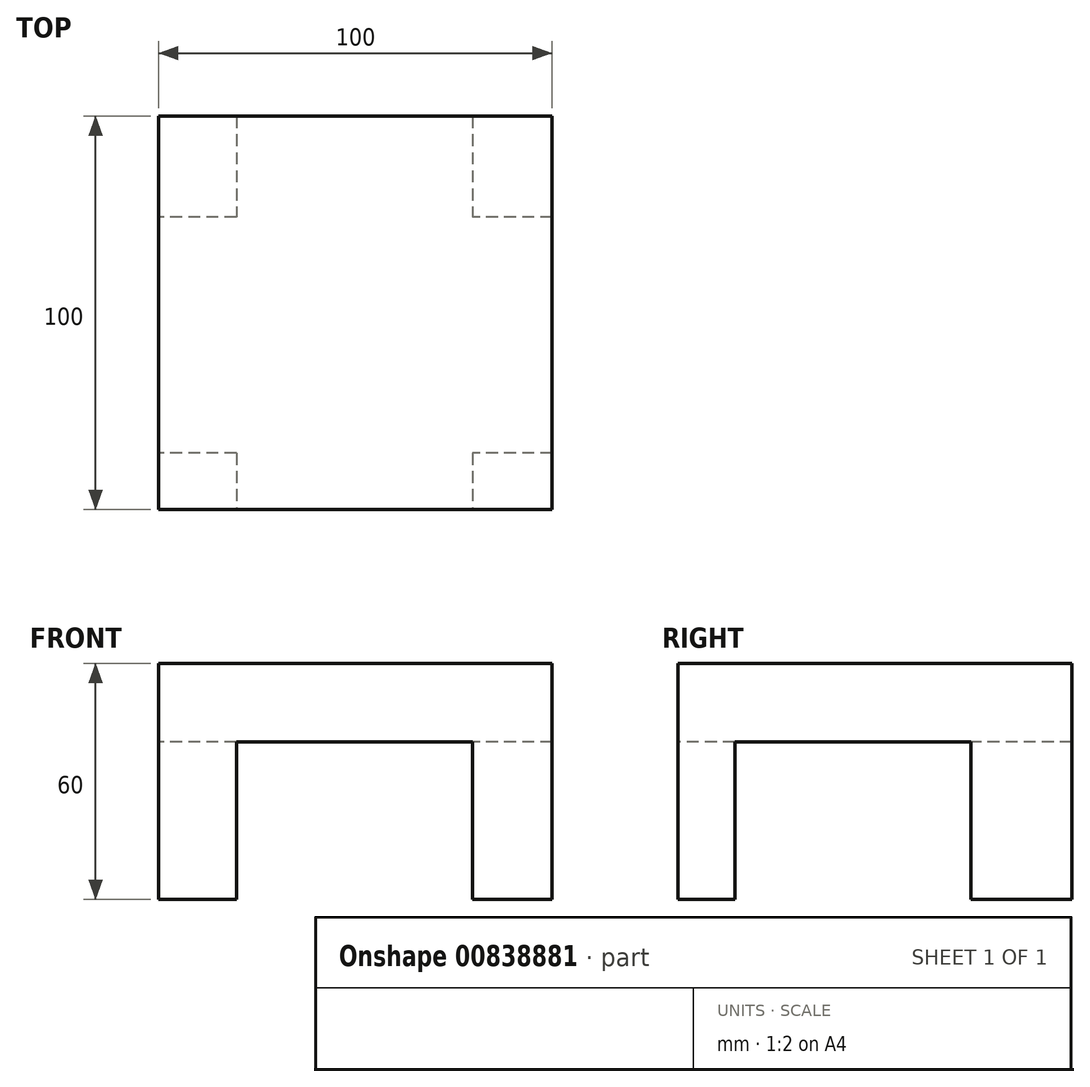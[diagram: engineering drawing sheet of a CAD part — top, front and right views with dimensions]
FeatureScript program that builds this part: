
annotation { "Feature Type Name" : "Feature", "Feature Type Description" : "" }
export const myFeature = defineFeature(function(context is Context, id is Id, definition is map)
    precondition{}
    {
        {
            var Q0;
            Q0=qCreatedBy(makeId("Top.planeOp"),FACE);
            var sketch = newSketch(context, id + "F0", { "sketchPlane" : qUnion([Q0])});
            skLineSegment(sketch, "E0.bottom", {"start": v(50, -50) * mm, "end": v(-50, -50) * mm});
            skLineSegment(sketch, "E0.top", {"start": v(50, 50) * mm, "end": v(-50, 50) * mm});
            skLineSegment(sketch, "E0.left", {"start": v(50, -50) * mm, "end": v(50, 50) * mm});
            skLineSegment(sketch, "E0.right", {"start": v(-50, -50) * mm, "end": v(-50, 50) * mm});
            skPoint(sketch, "E0.middle", {"position": v(0, 0) * mm});
            skSolve(sketch);
        }
        {
            var Q0;
            Q0 = qSketchRegion(id + "F0", true);
            extrude(context, id + "F1", {"entities" : qUnion([Q0]), "depth" : 100 * mm, "offsetDistance" : 25 * mm});
        }
        {
            var Q0;
            Q0=makeQuery(id+"F1.opExtrude","CAP_FACE",FACE,{"disambiguationData":[OSD([sQuery(id+"F0.wireOp",EDGE,"E0.bottom"),sQuery(id+"F0.wireOp",EDGE,"E0.top"),sQuery(id+"F0.wireOp",EDGE,"E0.left"),sQuery(id+"F0.wireOp",EDGE,"E0.right")])],"isStart":false});
            var sketch = newSketch(context, id + "F2", { "sketchPlane" : qUnion([Q0])});
            skLineSegment(sketch, "E1.bottom", {"start": v(-50, -50) * mm, "end": v(50, -50) * mm});
            skLineSegment(sketch, "E1.top", {"start": v(-50, 50) * mm, "end": v(50, 50) * mm});
            skLineSegment(sketch, "E1.left", {"start": v(-50, -50) * mm, "end": v(-50, 50) * mm});
            skLineSegment(sketch, "E1.right", {"start": v(50, -50) * mm, "end": v(50, 50) * mm});
            skSolve(sketch);
        }
        {
            var Q0;
            Q0 = qSketchRegion(id + "F2", true);
            extrude(context, id + "F3", {"entities" : qUnion([Q0]), "operationType" : NewBodyOperationType.REMOVE, "oppositeDirection" : true, "depth" : 40 * mm, "offsetDistance" : 25 * mm});
        }
        {
            var Q0;
            Q0=makeQuery(id+"F1.opExtrude","SWEPT_FACE",FACE,{"disambiguationData":[OSD([sQuery(id+"F0.wireOp",EDGE,"E0.bottom")])]});
            var sketch = newSketch(context, id + "F4", { "sketchPlane" : qUnion([Q0])});
            skLineSegment(sketch, "E2.bottom", {"start": v(-30.23, 0) * mm, "end": v(29.77, 0) * mm});
            skLineSegment(sketch, "E2.top", {"start": v(-30.23, 40) * mm, "end": v(29.77, 40) * mm});
            skLineSegment(sketch, "E2.left", {"start": v(-30.23, 0) * mm, "end": v(-30.23, 40) * mm});
            skLineSegment(sketch, "E2.right", {"start": v(29.77, 0) * mm, "end": v(29.77, 40) * mm});
            skSolve(sketch);
        }
        {
            var Q0;
            Q0=makeQuery(id+"F4.imprint","IMPRINT",FACE,{"disambiguationData":[TD([[makeQuery(id+"F4.imprint","IMPRINT",EDGE,{"derivedFrom":sQuery(id+"F4.wireOp",EDGE,"E2.bottom")}),-1.0]])]});
            extrude(context, id + "F5", {"entities" : qUnion([Q0]), "operationType" : NewBodyOperationType.REMOVE, "oppositeDirection" : true, "depth" : 176 * mm, "offsetDistance" : 25 * mm});
        }
        {
            var Q0;
            Q0=makeQuery(id+"F1.opExtrude","SWEPT_FACE",FACE,{"disambiguationData":[OSD([sQuery(id+"F0.wireOp",EDGE,"E0.right")])]});
            var sketch = newSketch(context, id + "F6", { "sketchPlane" : qUnion([Q0])});
            skLineSegment(sketch, "E3.bottom", {"start": v(35.6, 0) * mm, "end": v(-24.4, 0) * mm});
            skLineSegment(sketch, "E3.top", {"start": v(35.6, 40) * mm, "end": v(-24.4, 40) * mm});
            skLineSegment(sketch, "E3.left", {"start": v(35.6, 0) * mm, "end": v(35.6, 40) * mm});
            skLineSegment(sketch, "E3.right", {"start": v(-24.4, 0) * mm, "end": v(-24.4, 40) * mm});
            skSolve(sketch);
        }
        {
            var Q0;
            Q0 = qSketchRegion(id + "F6", true);
            extrude(context, id + "F7", {"entities" : qUnion([Q0]), "operationType" : NewBodyOperationType.REMOVE, "oppositeDirection" : true, "depth" : 223 * mm, "offsetDistance" : 25 * mm});
        }
    });
